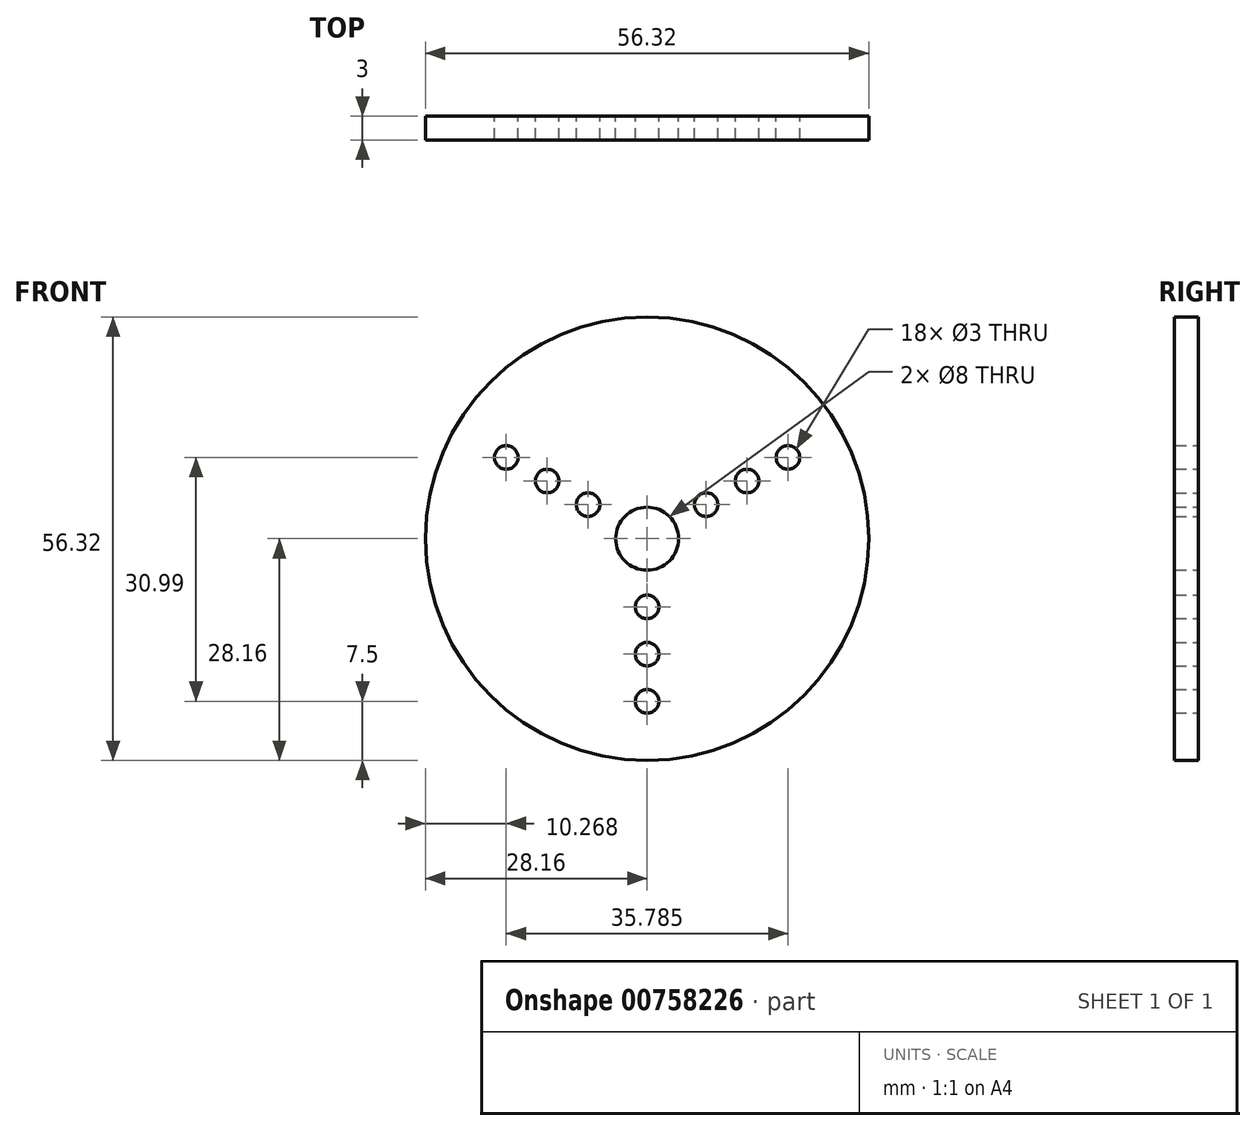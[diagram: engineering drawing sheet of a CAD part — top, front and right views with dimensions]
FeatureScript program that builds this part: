
annotation { "Feature Type Name" : "Feature", "Feature Type Description" : "" }
export const myFeature = defineFeature(function(context is Context, id is Id, definition is map)
    precondition{}
    {
        {
            var Q0;
            Q0=qCreatedBy(makeId("Front.planeOp"),FACE);
            var sketch = newSketch(context, id + "F0", { "sketchPlane" : qUnion([Q0])});
            skCircle(sketch, "E0.cCircle", {"center": v(0, 0) * mm, "radius": 4.33 * mm, "construction": true});
            skLineSegment(sketch, "E0.0", {"start": v(-7.5, 4.33) * mm, "end": v(7.5, 4.33) * mm, "construction": true});
            skLineSegment(sketch, "E0.1", {"start": v(7.5, 4.33) * mm, "end": v(0, -8.66) * mm, "construction": true});
            skLineSegment(sketch, "E0.2", {"start": v(0, -8.66) * mm, "end": v(-7.5, 4.33) * mm, "construction": true});
            skPoint(sketch, "E0.0.midPoint", {"position": v(0, 4.33) * mm});
            skCircle(sketch, "E1", {"center": v(7.5, 4.33) * mm, "radius": 1.5 * mm});
            skCircle(sketch, "E2", {"center": v(0, -8.66) * mm, "radius": 1.5 * mm});
            skCircle(sketch, "E3", {"center": v(-7.5, 4.33) * mm, "radius": 1.5 * mm});
            skCircle(sketch, "E4.cCircle", {"center": v(0, 0) * mm, "radius": 7.33 * mm, "construction": true});
            skLineSegment(sketch, "E4.0", {"start": v(-12.7, 7.33) * mm, "end": v(12.7, 7.33) * mm, "construction": true});
            skLineSegment(sketch, "E4.1", {"start": v(12.7, 7.33) * mm, "end": v(0, -14.66) * mm, "construction": true});
            skLineSegment(sketch, "E4.2", {"start": v(0, -14.66) * mm, "end": v(-12.7, 7.33) * mm, "construction": true});
            skPoint(sketch, "E4.0.midPoint", {"position": v(0, 7.33) * mm});
            skCircle(sketch, "E5", {"center": v(12.7, 7.33) * mm, "radius": 1.5 * mm});
            skCircle(sketch, "E6", {"center": v(-12.7, 7.33) * mm, "radius": 1.5 * mm});
            skCircle(sketch, "E7", {"center": v(0, -14.66) * mm, "radius": 1.5 * mm});
            skCircle(sketch, "E8.cCircle", {"center": v(0, 0) * mm, "radius": 10.33 * mm, "construction": true});
            skLineSegment(sketch, "E8.0", {"start": v(-17.9, 10.33) * mm, "end": v(17.9, 10.33) * mm, "construction": true});
            skLineSegment(sketch, "E8.1", {"start": v(17.9, 10.33) * mm, "end": v(0, -20.66) * mm, "construction": true});
            skLineSegment(sketch, "E8.2", {"start": v(0, -20.66) * mm, "end": v(-17.9, 10.33) * mm, "construction": true});
            skPoint(sketch, "E8.0.midPoint", {"position": v(0, 10.33) * mm});
            skCircle(sketch, "E9", {"center": v(17.9, 10.33) * mm, "radius": 1.5 * mm});
            skCircle(sketch, "E10", {"center": v(-17.9, 10.33) * mm, "radius": 1.5 * mm});
            skCircle(sketch, "E11", {"center": v(0, -20.66) * mm, "radius": 1.5 * mm});
            skCircle(sketch, "E12", {"center": v(0, 0) * mm, "radius": 4 * mm});
            skCircle(sketch, "E13", {"center": v(0, 0) * mm, "radius": 28.16 * mm});
            skSolve(sketch);
        }
        {
            var Q0;
            Q0 = qSketchRegion(id + "F0", true);
            extrude(context, id + "F1", {"entities" : qUnion([Q0]), "depth" : 3 * mm, "offsetDistance" : 25 * mm});
        }
    });
